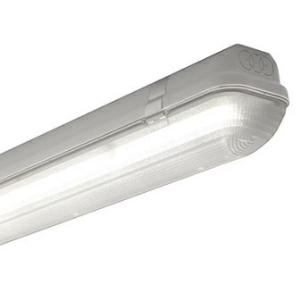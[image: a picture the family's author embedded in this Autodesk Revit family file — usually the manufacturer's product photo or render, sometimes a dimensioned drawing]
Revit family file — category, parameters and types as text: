
# Revit family: 3f_filippi_-_3f_linda_3f_filippi_-_58611_-_3f_linda_led_1x30w_ep_l1570
name_source: partatom
category: Lighting Fixtures
units: mm (PartAtom-declared; Revit-internal decimal feet)

## family parameters
Cut with Voids When Loaded = No
Host = Face
Light Source = No
Part Type = Normal
Room Calculation Point = No
Round Connector Dimension = Use Diameter
Shared = No

## types (1)
- 3F Filippi - 3F Linda (1 x LED, 5180 lm, 34.5 W, 4000 K)
    Apparent Load = 35 VA
    Approval mark = ENEC
    CIE Flux Codes = 44 77 94 97 100
    Color Rendering = 80
    Color Temperature = 4000 K
    Control Gear = Electronic ballast
    Default Elevation = 1800 mm
    Description = ILLUMINOTECHNICAL
Luminous efficiency 100% (DLOR 97%, ULOR 3%).
Initial luminous flux of the luminaire 5180 lm.
Emergency luminaire luminous flux BLF 11.4%.
Controlled symmetric distribution.
Installation Interdistance Transv.D = 1.77 x hu - Long.D = 1.17 x hu.
Tabular UGR (CIE 117 - 4H-8H; S=0.25H; 70/50/20): RUG 22.1 - 23.1.
Beam angle: 109° - 64°.
Luminous efficacy 150 lm/W.
Lifetime (L93/B10): 30000 h. (tq+25°C)
Lifetime (L90/B10): 50000 h. (tq+25°C)
Lifetime (L85/B10): 80000 h. (tq+25°C)
Lifetime (L80/B10): 100000 h. (tq+25°C)
Sudden decreased luminous flux after 50000 hours: 0% (C0).
Photobiological safety in compliance with IEC/TR 62778: RG0 risk exempt, (IEC 62471).
In compliance with IEC/EN 62722-2-1 - IEC/EN 62717 standards.

SOURCE
Linear LED module 30W/840.
Energy efficiency class (UE 2019/2020 - UE 2019/2015): D.
CIE 13.3 Colour rendering index: CRI >80 (R9 <50%).
IES TM-30 Fidelity Index: Rf = 84 Rg = 95.
CCT nominal colour temperature 4000 K.
Colour initial tolerance (MacAdam): SDCM 3.

MECHANICAL
Self-extinguishing V2 polycarbonate housing, injection moulded, RAL 7035 grey.
Ecologic anti-aging injected sealing gasket.
Diffuser in self-extinguishing V2 polycarbonate, photo-engraved interior, UV stabilised, injection moulded with smooth outer surface, tamper-proof opening.
Gear-holder reflector in hot-dip galvanised steel, painted with white polyester base.
Snug fit safety snap-lock clips for diffuser mounting in stainless steel, screwdriver opening.
Fixing brackets in stainless steel.
Possibility for technicians to access the interior of the luminaire.
Luminaire with limited surface temperature. - D - (EN 60598-2-24)
Dimensions: 1570x100 mm, height 100 mm. Weight 2.88 kg.
IP66 protection degree.
Mechanical strength to impacts IK10 (20 joule).
Glow-wire test resistance 850°C.

ELECTRICAL
Halogen Free electronic wiring 230V-50/60Hz, power factor 0.90, THD <25%, constant output current, SELV, class I, 1 driver.
Power of the luminaire 34.5 W.
CE - IEC 60598-1 - EN 60598-1.
EP maintained emergency wiring on board, 1h duration, 24h recharge; compliant with EN 60598-2-22, excluding high risk areas.
SAFE FLICKER: PstLM=<1 and SVM=<0.4 (IEC TR 61547-1 and IEC TR 63158), to ensure a more comfortable and safe light.
Ambient temperature from +5°C to +25°C.
Temperature class T6 max 85°C.
Relative humidity UR: <85%.

INSTALLATION
Ceiling / Suspended / Wall.
All accessories dedicated to this product are available on the Catalog and on our website www.3F-Filippi.com.

APPLICATIONS
Suitable product for food production plants (HACCP), IFS (Food Version 6), BRC (GSFS Food Version 7).
Dry, dusty indoor environments, subject to occasional water splashes.
Virtually shatterproof polycarbonate compatibly with the fumes / atmospheres that compromise the elasticity of plastic materials.
Not suitable for installation on surfaces subject to important vibrations, exposed to weather conditions, on ropes or poles.
Suitable for illumination of public car parks and parking grounds referred to DIN 67528:2018-04.

WARNING
Fixture not suitable for cold stores with an ambient temperature <5°C and/or relative humidity >85%.
Luminaire designed for disposal/recycling at end-of-life.
Replaceable (LED only) light source by a professional. Replaceable control gear by a professional.
    Height = 100 mm  [stored 0.328084 ft]
    Lamp = 1 x LED
    Lamp Light Flux = 5180 lm
    Lamp Power = 34.5 W
    Lamp count = 1
    Length = 1570 mm
    Lifetime = 50000 h
    Luminous efficacy = 150 lm/W
    Manufacturer = 3F Filippi
    ModVariant = No
    Model = 3F Filippi - 58611 - 3F Linda LED 1x30W EP L1570
    Mounting Place = Ceiling
    Mounting Type = Pendant
    Number of Poles = 1
    OnlyDefault = Yes
    Power Factor = 1
    Product Name = 3F Filippi - 3F Linda
    Product group = pendant luminaire
    ProductGroupID = 9
    Protection Class = Protection class I
    Protection Degree = IP 66
    RLX_Detail_Level = 1
    RLX_Emergency_Light_Flux = 0 lm
    RLX_Emergency_Type = 0
    RLX_Emergency_Type_DB = No
    RlxData = <blob elided: 68281 chars, md5=8dc2dc74>
    Socket = socket
    Standby Power = 0 W
    System Light Flux = 5180 lm
    System Power = 35 W
    Type Comments = Product without accessories
    Type Image = 3ffilippi_3f_linda_led_1x.jpg
    URL = http://relux.com
    VarID = ---
    Voltage = 0 V
    Weight = 0.00 kg
    Width = 100 mm  [stored 0.328084 ft]

note: [stored X ft] marks values corroborated as IEEE doubles in the binary element streams (Revit-internal decimal feet)

## geometry (parser evidence)
native form markers: Blend x4, Sweep x9
no freeform markers — native parametric forms only
